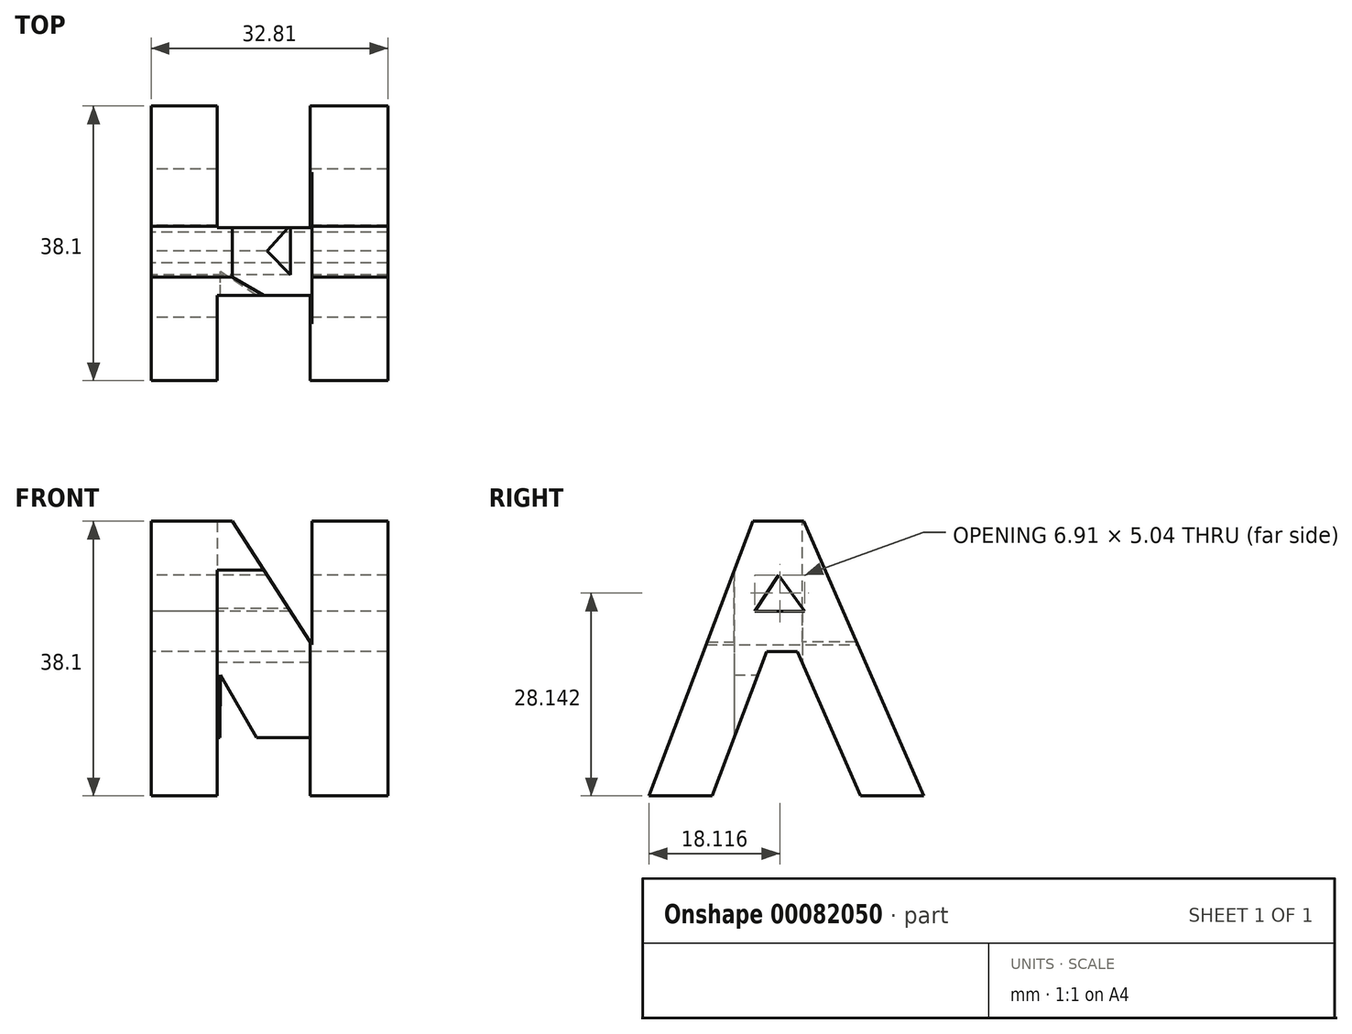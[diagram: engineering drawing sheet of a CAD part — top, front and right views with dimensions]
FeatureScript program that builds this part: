
annotation { "Feature Type Name" : "Feature", "Feature Type Description" : "" }
export const myFeature = defineFeature(function(context is Context, id is Id, definition is map)
    precondition{}
    {
        {
            var Q0;
            Q0=qCreatedBy(makeId("Front.planeOp"),FACE);
            var sketch = newSketch(context, id + "F0", { "sketchPlane" : qUnion([Q0])});
            skLineSegment(sketch, "E0", {"start": v(0, 0) * mm, "end": v(38.1, 0) * mm});
            skLineSegment(sketch, "E1", {"start": v(38.1, 0) * mm, "end": v(38.1, 38.1) * mm});
            skLineSegment(sketch, "E2", {"start": v(38.1, 38.1) * mm, "end": v(0, 38.1) * mm});
            skLineSegment(sketch, "E3", {"start": v(0, 38.1) * mm, "end": v(0, 0) * mm});
            skSolve(sketch);
        }
        {
            var Q0;
            Q0 = qSketchRegion(id + "F0", true);
            extrude(context, id + "F1", {"entities" : qUnion([Q0]), "depth" : 38.1 * mm});
        }
        {
            var Q0;
            Q0=qCreatedBy(makeId("Right.planeOp"),FACE);
            var sketch = newSketch(context, id + "F2", { "sketchPlane" : qUnion([Q0])});
            skLineSegment(sketch, "E4", {"start": v(0, 0) * mm, "end": v(0, 38.1) * mm});
            skLineSegment(sketch, "E5", {"start": v(0, 38.1) * mm, "end": v(-38.1, 38.1) * mm});
            skLineSegment(sketch, "E6", {"start": v(-38.1, 38.1) * mm, "end": v(-38.1, 0) * mm});
            skLineSegment(sketch, "E7", {"start": v(-38.1, 0) * mm, "end": v(0, 0) * mm});
            skLineSegment(sketch, "E8", {"start": v(-38.1, 0) * mm, "end": v(-23.73, 38.1) * mm});
            skLineSegment(sketch, "E9", {"start": v(0, 0) * mm, "end": v(-16.67, 38.1) * mm});
            skLineSegment(sketch, "E10", {"start": v(-29.34, 0) * mm, "end": v(-21.78, 20.02) * mm});
            skLineSegment(sketch, "E11", {"start": v(-21.78, 20.02) * mm, "end": v(-17.52, 20.02) * mm});
            skLineSegment(sketch, "E12", {"start": v(-17.52, 20.02) * mm, "end": v(-8.76, 0) * mm});
            skLineSegment(sketch, "E13", {"start": v(-20.13, 25.62) * mm, "end": v(-16.53, 25.62) * mm});
            skLineSegment(sketch, "E14", {"start": v(-16.53, 25.62) * mm, "end": v(-20.13, 30.66) * mm});
            skLineSegment(sketch, "E15", {"start": v(-20.13, 30.66) * mm, "end": v(-23.44, 25.62) * mm});
            skLineSegment(sketch, "E16", {"start": v(-23.44, 25.62) * mm, "end": v(-20.13, 25.62) * mm});
            skSolve(sketch);
        }
        {
            var Q0;
            {var subQ0=sQuery(id+"F2.wireOp",EDGE,"E6");Q0=makeQuery(id+"F2.imprint","IMPRINT",FACE,{"disambiguationData":[TD([[makeQuery(id+"F2.imprint","IMPRINT",EDGE,{"derivedFrom":subQ0}),1.0]])]});}
            var Q1;
            {var subQ0=sQuery(id+"F2.wireOp",EDGE,"E10");Q1=makeQuery(id+"F2.imprint","IMPRINT",FACE,{"disambiguationData":[TD([[makeQuery(id+"F2.imprint","IMPRINT",EDGE,{"derivedFrom":subQ0}),-1.0]])]});}
            var Q2;
            {var subQ0=sQuery(id+"F2.wireOp",EDGE,"E4");Q2=makeQuery(id+"F2.imprint","IMPRINT",FACE,{"disambiguationData":[TD([[makeQuery(id+"F2.imprint","IMPRINT",EDGE,{"derivedFrom":subQ0}),1.0]])]});}
            var Q3;
            Q3=makeQuery(id+"F2.imprint","IMPRINT",FACE,{"disambiguationData":[TD([[makeQuery(id+"F2.imprint","IMPRINT",EDGE,{"derivedFrom":sQuery(id+"F2.wireOp",EDGE,"E13")}),1.0]])]});
            extrude(context, id + "F3", {"entities" : qUnion([Q0, Q1, Q2, Q3]), "operationType" : NewBodyOperationType.REMOVE, "depth" : 38.1 * mm});
        }
        {
            var Q0;
            Q0=qCreatedBy(makeId("Front.planeOp"),FACE);
            var sketch = newSketch(context, id + "F4", { "sketchPlane" : qUnion([Q0])});
            skLineSegment(sketch, "E17", {"start": v(0, 0) * mm, "end": v(38.1, 0) * mm});
            skLineSegment(sketch, "E18", {"start": v(38.1, 0) * mm, "end": v(38.1, 38.1) * mm});
            skLineSegment(sketch, "E19", {"start": v(38.1, 38.1) * mm, "end": v(0, 38.1) * mm});
            skLineSegment(sketch, "E20", {"start": v(0, 38.1) * mm, "end": v(0, 0) * mm});
            skLineSegment(sketch, "E21", {"start": v(13.19, 38.1) * mm, "end": v(24.25, 20.99) * mm});
            skLineSegment(sketch, "E22", {"start": v(11.37, 0) * mm, "end": v(11.56, 16.82) * mm});
            skLineSegment(sketch, "E23", {"start": v(11.56, 16.82) * mm, "end": v(21.16, 0) * mm});
            skLineSegment(sketch, "E24", {"start": v(24.25, 20.99) * mm, "end": v(24.25, 38.1) * mm});
            skLineSegment(sketch, "E25", {"start": v(34.76, 38.1) * mm, "end": v(34.76, 0) * mm});
            skLineSegment(sketch, "E26", {"start": v(1.95, 38.1) * mm, "end": v(1.95, 0) * mm});
            skSolve(sketch);
        }
        {
            var Q0;
            {var subQ0=sQuery(id+"F4.wireOp",EDGE,"E18");Q0=makeQuery(id+"F4.imprint","IMPRINT",FACE,{"disambiguationData":[TD([[makeQuery(id+"F4.imprint","IMPRINT",EDGE,{"derivedFrom":subQ0}),1.0]])]});}
            var Q1;
            {var subQ0=sQuery(id+"F4.wireOp",EDGE,"E21");Q1=makeQuery(id+"F4.imprint","IMPRINT",FACE,{"disambiguationData":[TD([[makeQuery(id+"F4.imprint","IMPRINT",EDGE,{"derivedFrom":subQ0}),1.0]])]});}
            var Q2;
            {var subQ0=sQuery(id+"F4.wireOp",EDGE,"E22");Q2=makeQuery(id+"F4.imprint","IMPRINT",FACE,{"disambiguationData":[TD([[makeQuery(id+"F4.imprint","IMPRINT",EDGE,{"derivedFrom":subQ0}),-1.0]])]});}
            var Q3;
            {var subQ0=sQuery(id+"F4.wireOp",EDGE,"E20");Q3=makeQuery(id+"F4.imprint","IMPRINT",FACE,{"disambiguationData":[TD([[makeQuery(id+"F4.imprint","IMPRINT",EDGE,{"derivedFrom":subQ0}),1.0]])]});}
            extrude(context, id + "F5", {"entities" : qUnion([Q0, Q1, Q2, Q3]), "operationType" : NewBodyOperationType.REMOVE, "depth" : 38.1 * mm});
        }
        {
            var Q0;
            Q0=qCreatedBy(makeId("Top.planeOp"),FACE);
            var sketch = newSketch(context, id + "F6", { "sketchPlane" : qUnion([Q0])});
            skLineSegment(sketch, "E27", {"start": v(0, 0) * mm, "end": v(38.1, 0) * mm});
            skLineSegment(sketch, "E28", {"start": v(38.1, 0) * mm, "end": v(38.1, -38.1) * mm});
            skLineSegment(sketch, "E29", {"start": v(38.1, -38.1) * mm, "end": v(0, -38.1) * mm});
            skLineSegment(sketch, "E30", {"start": v(0, -38.1) * mm, "end": v(0, 0) * mm});
            skLineSegment(sketch, "E31", {"start": v(11.12, 0) * mm, "end": v(11.12, -16.86) * mm});
            skLineSegment(sketch, "E32", {"start": v(11.12, -16.86) * mm, "end": v(24, -16.86) * mm});
            skLineSegment(sketch, "E33", {"start": v(24, -16.86) * mm, "end": v(24, 0) * mm});
            skLineSegment(sketch, "E34", {"start": v(11.12, -38.1) * mm, "end": v(11.12, -26.29) * mm});
            skLineSegment(sketch, "E35", {"start": v(11.12, -26.29) * mm, "end": v(24, -26.29) * mm});
            skLineSegment(sketch, "E36", {"start": v(24, -26.29) * mm, "end": v(24, -38.1) * mm});
            skLineSegment(sketch, "E37", {"start": v(34.93, 0) * mm, "end": v(34.93, -38.1) * mm});
            skLineSegment(sketch, "E38", {"start": v(1.93, 0) * mm, "end": v(1.93, -38.1) * mm});
            skSolve(sketch);
        }
        {
            var Q0;
            {var subQ0=sQuery(id+"F6.wireOp",EDGE,"E30");Q0=makeQuery(id+"F6.imprint","IMPRINT",FACE,{"disambiguationData":[TD([[makeQuery(id+"F6.imprint","IMPRINT",EDGE,{"derivedFrom":subQ0}),-1.0]])]});}
            var Q1;
            {var subQ0=sQuery(id+"F6.wireOp",EDGE,"E31");Q1=makeQuery(id+"F6.imprint","IMPRINT",FACE,{"disambiguationData":[TD([[makeQuery(id+"F6.imprint","IMPRINT",EDGE,{"derivedFrom":subQ0}),1.0]])]});}
            var Q2;
            {var subQ0=sQuery(id+"F6.wireOp",EDGE,"E34");Q2=makeQuery(id+"F6.imprint","IMPRINT",FACE,{"disambiguationData":[TD([[makeQuery(id+"F6.imprint","IMPRINT",EDGE,{"derivedFrom":subQ0}),-1.0]])]});}
            var Q3;
            {var subQ0=sQuery(id+"F6.wireOp",EDGE,"E28");Q3=makeQuery(id+"F6.imprint","IMPRINT",FACE,{"disambiguationData":[TD([[makeQuery(id+"F6.imprint","IMPRINT",EDGE,{"derivedFrom":subQ0}),-1.0]])]});}
            extrude(context, id + "F7", {"entities" : qUnion([Q0, Q1, Q2, Q3]), "operationType" : NewBodyOperationType.REMOVE, "depth" : 38.1 * mm});
        }
    });
